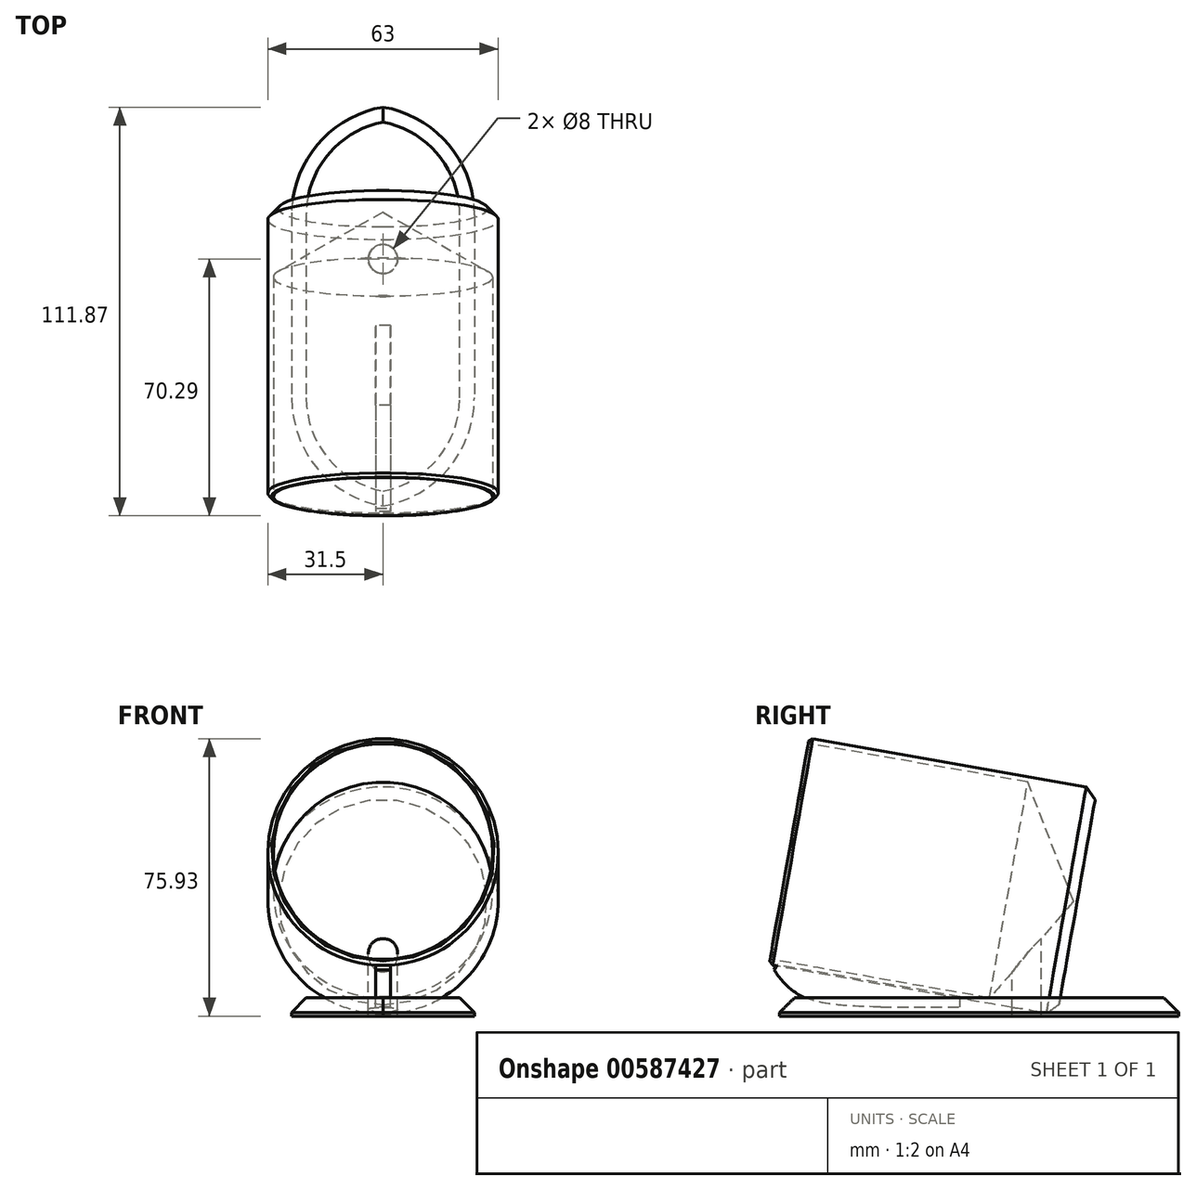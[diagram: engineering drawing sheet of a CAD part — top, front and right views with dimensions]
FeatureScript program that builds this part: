
annotation { "Feature Type Name" : "Feature", "Feature Type Description" : "" }
export const myFeature = defineFeature(function(context is Context, id is Id, definition is map)
    precondition{}
    {
        {
            var Q0;
            Q0=qCreatedBy(makeId("Right.planeOp"),FACE);
            var sketch = newSketch(context, id + "F0", { "sketchPlane" : qUnion([Q0])});
            skLineSegment(sketch, "E0.bottom", {"start": v(55, -2.5) * mm, "end": v(-55, -2.5) * mm});
            skLineSegment(sketch, "E0.top", {"start": v(55, 2.5) * mm, "end": v(-55, 2.5) * mm});
            skLineSegment(sketch, "E0.left", {"start": v(55, -2.5) * mm, "end": v(55, 2.5) * mm});
            skLineSegment(sketch, "E0.right", {"start": v(-55, -2.5) * mm, "end": v(-55, 2.5) * mm});
            skPoint(sketch, "E0.middle", {"position": v(0, 0) * mm});
            skSolve(sketch);
        }
        {
            var Q0;
            Q0 = qSketchRegion(id + "F0", true);
            extrude(context, id + "F1", {"entities" : qUnion([Q0]), "endBound" : BoundingType.SYMMETRIC, "depth" : 50 * mm, "offsetDistance" : 25 * mm});
        }
        {
            var Q0;
            Q0=makeQuery(id+"F1.opExtrude","SWEPT_EDGE",EDGE,{"disambiguationData":[OSD([sQuery(id+"F0.wireOp",EDGE,"E0.top"),sQuery(id+"F0.wireOp",EDGE,"E0.right")])]});
            cPlane(context, id + "F2", {"entities" : qUnion([Q0]), "cplaneType" : CPlaneType.LINE_ANGLE, "offset" : 0 * mm, "angle" : 10 * degree, "width" : 150 * mm, "height" : 150 * mm});
        }
        {
            var Q0;
            Q0=qCreatedBy(id+"F2.planeOp",FACE);
            var sketch = newSketch(context, id + "F3", { "sketchPlane" : qUnion([Q0])});
            skCircle(sketch, "E1", {"center": v(0, 32.91) * mm, "radius": 31.5 * mm});
            skSolve(sketch);
        }
        {
            var Q0;
            Q0=makeQuery(id+"F3.imprint","IMPRINT",FACE,{"disambiguationData":[TD([[makeQuery(id+"F3.imprint","IMPRINT",EDGE,{"derivedFrom":sQuery(id+"F3.wireOp",EDGE,"E1")}),1.0]])]});
            var Q1;
            Q1=makeQuery(id+"F1.opExtrude","SWEPT_FACE",FACE,{"disambiguationData":[OSD([sQuery(id+"F0.wireOp",EDGE,"E0.bottom")])]});
            var Q2;
            Q2=makeQuery(id+"F1.opExtrude","SWEPT_BODY",BODY,{"disambiguationData":[OSD([sQuery(id+"F0.wireOp",EDGE,"E0.bottom"),sQuery(id+"F0.wireOp",EDGE,"E0.top"),sQuery(id+"F0.wireOp",EDGE,"E0.left"),sQuery(id+"F0.wireOp",EDGE,"E0.right")])]});
            extrude(context, id + "F4", {"entities" : qUnion([Q0]), "oppositeDirection" : true, "depth" : 76 * mm, "endBoundEntityFace" : qUnion([Q1]), "endBoundEntityBody" : qUnion([Q2]), "offsetDistance" : 45 * mm, "hasSecondDirection" : true, "secondDirectionOppositeDirection" : false, "secondDirectionDepth" : 4 * mm});
        }
        {
            var Q0;
            Q0=sQuery(id+"F3.wireOp",VERTEX,"E1.center");
            var Q1;
            Q1=makeQuery(id+"F1.opExtrude","SWEPT_BODY",BODY,{"disambiguationData":[OSD([sQuery(id+"F0.wireOp",EDGE,"E0.bottom"),sQuery(id+"F0.wireOp",EDGE,"E0.top"),sQuery(id+"F0.wireOp",EDGE,"E0.left"),sQuery(id+"F0.wireOp",EDGE,"E0.right")])]});
            var Q2;
            Q2=makeQuery(id+"F4.opExtrude","SWEPT_BODY",BODY,{"disambiguationData":[OSD([sQuery(id+"F3.wireOp",EDGE,"E1")])]});
            hole(context, id + "F5", {"style" : HoleStyle.SIMPLE, "endStyle" : HoleEndStyle.BLIND, "holeDiameter" : 60 * mm, "majorDiameter" : 5 * mm, "holeDepth" : 57 * mm, "isTappedThrough" : true, "tappedDepth" : 12 * mm, "tapClearance" : 3, "startFromSketch" : true, "locations" : qUnion([Q0]), "scope" : qUnion([Q1, Q2])});
        }
        {
            var Q0;
            Q0=sQuery(id+"F3.wireOp",VERTEX,"E1.center");
            var Q1;
            Q1=makeQuery(id+"F4.opExtrude","SWEPT_BODY",BODY,{"disambiguationData":[OSD([sQuery(id+"F3.wireOp",EDGE,"E1")])]});
            hole(context, id + "F6", {"style" : HoleStyle.SIMPLE, "endStyle" : HoleEndStyle.BLIND, "oppositeDirection" : true, "holeDiameter" : 60 * mm, "majorDiameter" : 5 * mm, "holeDepth" : 45 * mm, "isTappedThrough" : true, "tappedDepth" : 12 * mm, "tapClearance" : 3, "startFromSketch" : true, "locations" : qUnion([Q0]), "scope" : qUnion([Q1])});
        }
        {
            var Q0;
            Q0=qCreatedBy(makeId("Top.planeOp"),FACE);
            var sketch = newSketch(context, id + "F7", { "sketchPlane" : qUnion([Q0])});
            skPoint(sketch, "E2", {"position": v(0, 13) * mm});
            skSolve(sketch);
        }
        {
            var Q0;
            Q0=sQuery(id+"F7.wireOp",VERTEX,"E2");
            var Q1;
            Q1=makeQuery(id+"F1.opExtrude","SWEPT_BODY",BODY,{"disambiguationData":[OSD([sQuery(id+"F0.wireOp",EDGE,"E0.bottom"),sQuery(id+"F0.wireOp",EDGE,"E0.top"),sQuery(id+"F0.wireOp",EDGE,"E0.left"),sQuery(id+"F0.wireOp",EDGE,"E0.right")])]});
            var Q2;
            Q2=makeQuery(id+"F4.opExtrude","SWEPT_BODY",BODY,{"disambiguationData":[OSD([sQuery(id+"F3.wireOp",EDGE,"E1")])]});
            hole(context, id + "F8", {"style" : HoleStyle.SIMPLE, "endStyle" : HoleEndStyle.BLIND, "holeDiameter" : 8 * mm, "majorDiameter" : 5 * mm, "holeDepth" : 47 * mm, "isTappedThrough" : true, "tappedDepth" : 12 * mm, "tapClearance" : 3, "startFromSketch" : true, "locations" : qUnion([Q0]), "scope" : qUnion([Q1, Q2])});
        }
        {
            var Q0;
            Q0=qCreatedBy(makeId("Right.planeOp"),FACE);
            var sketch = newSketch(context, id + "F9", { "sketchPlane" : qUnion([Q0])});
            skFitSpline(sketch, "E3", {"points": [v(-26.97, 0) * mm, v(-48.8, 3.07) * mm, v(-57.32, 11.88) * mm], "startDerivative": vector(-43.32, 0.98) * mm, "endDerivative": vector(-16.05, 23.9) * mm});
            skLineSegment(sketch, "E4", {"start": v(-5.18, 0) * mm, "end": v(-5.18, 2.8) * mm});
            skLineSegment(sketch, "E5", {"start": v(-5.18, 2.8) * mm, "end": v(-57.32, 11.88) * mm});
            skLineSegment(sketch, "E6", {"start": v(-26.97, 0) * mm, "end": v(-5.18, 0) * mm});
            skSolve(sketch);
        }
        {
            var Q0;
            Q0=makeQuery(id+"F9.imprint","IMPRINT",FACE,{"disambiguationData":[TD([[makeQuery(id+"F9.imprint","IMPRINT",EDGE,{"derivedFrom":sQuery(id+"F9.wireOp",EDGE,"E3")}),-1.0]])]});
            extrude(context, id + "F10", {"entities" : qUnion([Q0]), "endBound" : BoundingType.SYMMETRIC, "depth" : 4 * mm, "offsetDistance" : 25 * mm});
        }
        {
            var Q0;
            Q0=makeQuery(id+"F1.opExtrude","CAP_EDGE",EDGE,{"disambiguationData":[OSD([sQuery(id+"F0.wireOp",EDGE,"E0.right")])],"isStart":true});
            var Q1;
            Q1=makeQuery(id+"F1.opExtrude","CAP_EDGE",EDGE,{"disambiguationData":[OSD([sQuery(id+"F0.wireOp",EDGE,"E0.right")])],"isStart":false});
            var Q2;
            Q2=makeQuery(id+"F1.opExtrude","CAP_EDGE",EDGE,{"disambiguationData":[OSD([sQuery(id+"F0.wireOp",EDGE,"E0.left")])],"isStart":true});
            var Q3;
            Q3=makeQuery(id+"F1.opExtrude","CAP_EDGE",EDGE,{"disambiguationData":[OSD([sQuery(id+"F0.wireOp",EDGE,"E0.left")])],"isStart":false});
            fillet(context, id + "F11", {"entities" : qUnion([Q0, Q1, Q2, Q3]), "radius" : 30 * mm, "tangentPropagation" : true, "allowEdgeOverflow" : false});
        }
        {
            var Q0;
            Q0=makeQuery(id+"F4.opExtrude","CAP_EDGE",EDGE,{"disambiguationData":[OSD([sQuery(id+"F3.wireOp",EDGE,"E1")])],"isStart":false});
            chamfer(context, id + "F12", {"entities" : qUnion([Q0]), "width" : 3 * mm, "tangentPropagation" : true});
        }
        {
            var Q0;
            Q0=makeQuery(id+"F4.opExtrude","CAP_EDGE",EDGE,{"disambiguationData":[OSD([sQuery(id+"F3.wireOp",EDGE,"E1")])],"isStart":true});
            chamfer(context, id + "F13", {"entities" : qUnion([Q0]), "width" : 1 * mm, "tangentPropagation" : true});
        }
        {
            var Q0;
            Q0=makeQuery(id+"F11.opFillet","BLEND_EDGE",EDGE,{"blendedFrom":[makeQuery(id+"F1.opExtrude","CAP_EDGE",EDGE,{"disambiguationData":[OSD([sQuery(id+"F0.wireOp",EDGE,"E0.right")])],"isStart":false}),makeQuery(id+"F1.opExtrude","SWEPT_FACE",FACE,{"disambiguationData":[OSD([sQuery(id+"F0.wireOp",EDGE,"E0.top")])]})],"blendedInto":[makeQuery(id+"F1.opExtrude","SWEPT_FACE",FACE,{"disambiguationData":[OSD([sQuery(id+"F0.wireOp",EDGE,"E0.top")])]})]});
            var Q1;
            Q1=makeQuery(id+"F1.opExtrude","CAP_EDGE",EDGE,{"disambiguationData":[OSD([sQuery(id+"F0.wireOp",EDGE,"E0.top")])],"isStart":false});
            var Q2;
            Q2=makeQuery(id+"F11.opFillet","BLEND_EDGE",EDGE,{"blendedFrom":[makeQuery(id+"F1.opExtrude","CAP_EDGE",EDGE,{"disambiguationData":[OSD([sQuery(id+"F0.wireOp",EDGE,"E0.left")])],"isStart":false}),makeQuery(id+"F1.opExtrude","SWEPT_FACE",FACE,{"disambiguationData":[OSD([sQuery(id+"F0.wireOp",EDGE,"E0.top")])]})],"blendedInto":[makeQuery(id+"F1.opExtrude","SWEPT_FACE",FACE,{"disambiguationData":[OSD([sQuery(id+"F0.wireOp",EDGE,"E0.top")])]})]});
            var Q3;
            Q3=makeQuery(id+"F11.opFillet","BLEND_EDGE",EDGE,{"blendedFrom":[makeQuery(id+"F1.opExtrude","CAP_EDGE",EDGE,{"disambiguationData":[OSD([sQuery(id+"F0.wireOp",EDGE,"E0.left")])],"isStart":true}),makeQuery(id+"F1.opExtrude","SWEPT_FACE",FACE,{"disambiguationData":[OSD([sQuery(id+"F0.wireOp",EDGE,"E0.top")])]})],"blendedInto":[makeQuery(id+"F1.opExtrude","SWEPT_FACE",FACE,{"disambiguationData":[OSD([sQuery(id+"F0.wireOp",EDGE,"E0.top")])]})]});
            var Q4;
            Q4=makeQuery(id+"F1.opExtrude","CAP_EDGE",EDGE,{"disambiguationData":[OSD([sQuery(id+"F0.wireOp",EDGE,"E0.top")])],"isStart":true});
            var Q5;
            Q5=makeQuery(id+"F11.opFillet","BLEND_EDGE",EDGE,{"blendedFrom":[makeQuery(id+"F1.opExtrude","CAP_EDGE",EDGE,{"disambiguationData":[OSD([sQuery(id+"F0.wireOp",EDGE,"E0.right")])],"isStart":true}),makeQuery(id+"F1.opExtrude","SWEPT_FACE",FACE,{"disambiguationData":[OSD([sQuery(id+"F0.wireOp",EDGE,"E0.top")])]})],"blendedInto":[makeQuery(id+"F1.opExtrude","SWEPT_FACE",FACE,{"disambiguationData":[OSD([sQuery(id+"F0.wireOp",EDGE,"E0.top")])]})]});
            chamfer(context, id + "F14", {"entities" : qUnion([Q0, Q1, Q2, Q3, Q4, Q5]), "width" : 4 * mm, "tangentPropagation" : true});
        }
        {
            var Q0;
            Q0=sQuery(id+"F7.wireOp",VERTEX,"E2");
            var Q1;
            Q1=makeQuery(id+"F1.opExtrude","SWEPT_BODY",BODY,{"disambiguationData":[OSD([sQuery(id+"F0.wireOp",EDGE,"E0.bottom"),sQuery(id+"F0.wireOp",EDGE,"E0.top"),sQuery(id+"F0.wireOp",EDGE,"E0.left"),sQuery(id+"F0.wireOp",EDGE,"E0.right")])]});
            var Q2;
            Q2=makeQuery(id+"F4.opExtrude","SWEPT_BODY",BODY,{"disambiguationData":[OSD([sQuery(id+"F3.wireOp",EDGE,"E1")])]});
            hole(context, id + "F15", {"style" : HoleStyle.SIMPLE, "endStyle" : HoleEndStyle.BLIND, "oppositeDirection" : true, "holeDiameter" : 8 * mm, "majorDiameter" : 5 * mm, "holeDepth" : 47 * mm, "isTappedThrough" : true, "tappedDepth" : 12 * mm, "tapClearance" : 3, "startFromSketch" : true, "locations" : qUnion([Q0]), "scope" : qUnion([Q1, Q2])});
        }
        {
            var Q0;
            Q0=makeQuery(id+"F10.opExtrude","SWEPT_EDGE",EDGE,{"disambiguationData":[OSD([sQuery(id+"F9.wireOp",EDGE,"E3"),sQuery(id+"F9.wireOp",EDGE,"E5")])]});
            chamfer(context, id + "F16", {"entities" : qUnion([Q0]), "width" : 0.9 * mm, "tangentPropagation" : true});
        }
    });
